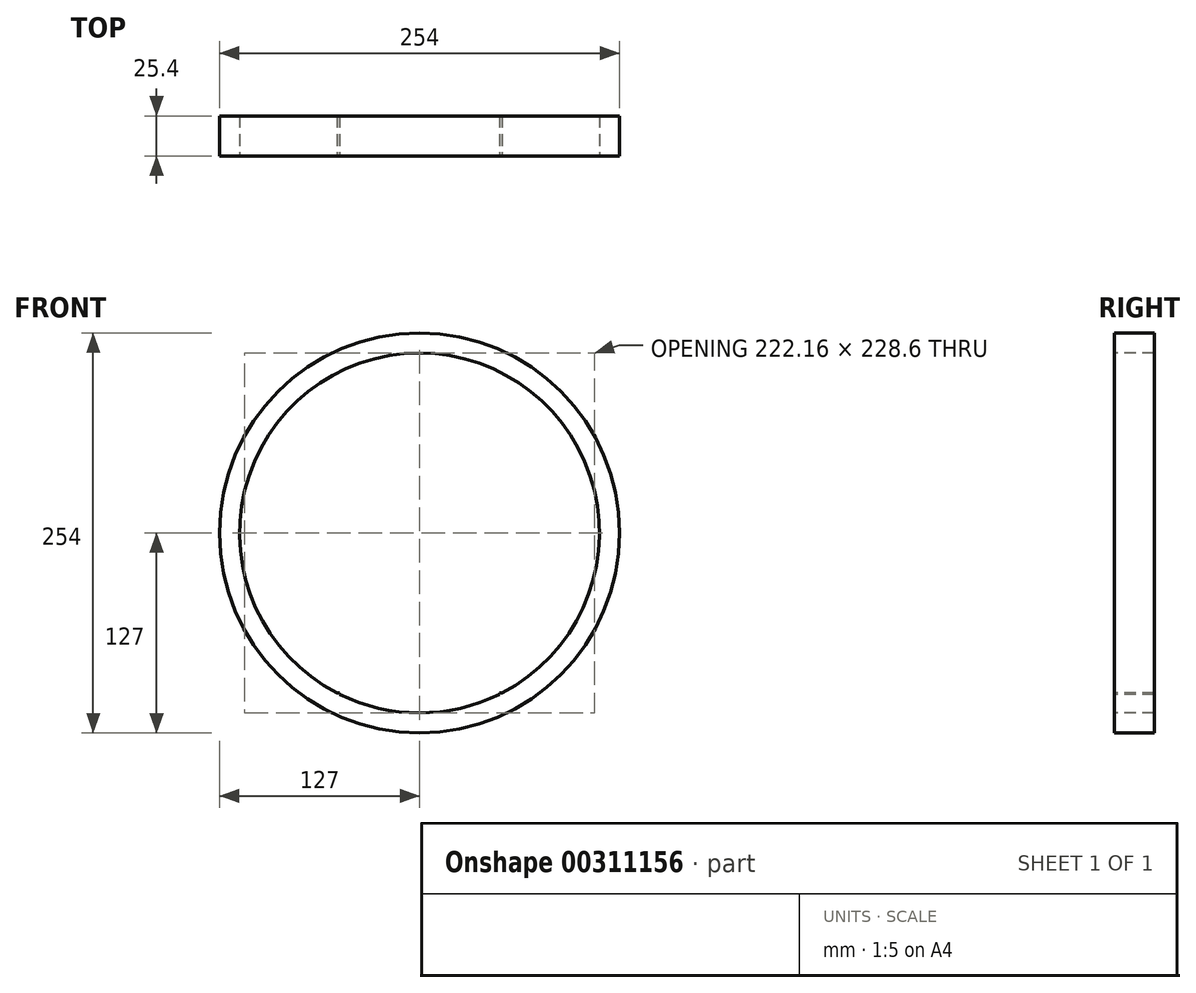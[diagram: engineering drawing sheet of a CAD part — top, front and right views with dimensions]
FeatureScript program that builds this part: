
annotation { "Feature Type Name" : "Feature", "Feature Type Description" : "" }
export const myFeature = defineFeature(function(context is Context, id is Id, definition is map)
    precondition{}
    {
        {
            var Q0;
            Q0=qCreatedBy(makeId("Front.planeOp"),FACE);
            var sketch = newSketch(context, id + "F0", { "sketchPlane" : qUnion([Q0])});
            skCircle(sketch, "E0", {"center": v(0, 0) * mm, "radius": 127 * mm});
            skSolve(sketch);
        }
        {
            var Q0;
            Q0=makeQuery(id+"F0.imprint","IMPRINT",FACE,{"disambiguationData":[TD([[makeQuery(id+"F0.imprint","IMPRINT",EDGE,{"derivedFrom":sQuery(id+"F0.wireOp",EDGE,"E0")}),1.0]])]});
            extrude(context, id + "F1", {"entities" : qUnion([Q0]), "depth" : 25.4 * mm});
        }
        {
            var Q0;
            Q0=makeQuery(id+"F1.opExtrude","CAP_FACE",FACE,{"disambiguationData":[OSD([sQuery(id+"F0.wireOp",EDGE,"E0")])],"isStart":false});
            var sketch = newSketch(context, id + "F2", { "sketchPlane" : qUnion([Q0])});
            skCircle(sketch, "E1", {"center": v(0, 0) * mm, "radius": 114.3 * mm});
            skLineSegment(sketch, "E2", {"start": v(0, 0) * mm, "end": v(25.4, 0) * mm});
            skLineSegment(sketch, "E3", {"start": v(25.4, 0) * mm, "end": v(50.8, 0) * mm});
            skLineSegment(sketch, "E4", {"start": v(50.8, 0) * mm, "end": v(76.2, 0) * mm});
            skLineSegment(sketch, "E5", {"start": v(76.2, 0) * mm, "end": v(101.6, 0) * mm});
            skLineSegment(sketch, "E6", {"start": v(101.6, 0) * mm, "end": v(114.3, 0) * mm});
            skLineSegment(sketch, "E7", {"start": v(25.4, 0) * mm, "end": v(25.4, -111.44) * mm});
            skLineSegment(sketch, "E8", {"start": v(25.4, 0) * mm, "end": v(25.4, 111.44) * mm});
            skLineSegment(sketch, "E9", {"start": v(50.8, 0) * mm, "end": v(50.8, 102.4) * mm});
            skLineSegment(sketch, "E10", {"start": v(50.8, 0) * mm, "end": v(50.8, -102.4) * mm});
            skLineSegment(sketch, "E11", {"start": v(76.2, 0) * mm, "end": v(76.2, 85.2) * mm});
            skLineSegment(sketch, "E12", {"start": v(76.2, 0) * mm, "end": v(76.2, -85.2) * mm});
            skLineSegment(sketch, "E13", {"start": v(101.6, 0) * mm, "end": v(101.6, 52.36) * mm});
            skLineSegment(sketch, "E14", {"start": v(101.6, 0) * mm, "end": v(101.6, -52.36) * mm});
            skPoint(sketch, "E15.orphan", {"position": v(0, 114.3) * mm});
            skLineSegment(sketch, "E16", {"start": v(0, 0) * mm, "end": v(0, 25.4) * mm});
            skLineSegment(sketch, "E17", {"start": v(0, 25.4) * mm, "end": v(0, 50.8) * mm});
            skLineSegment(sketch, "E18", {"start": v(0, 50.8) * mm, "end": v(0, 76.2) * mm});
            skLineSegment(sketch, "E19", {"start": v(0, 76.2) * mm, "end": v(0, 101.6) * mm});
            skLineSegment(sketch, "E20", {"start": v(0, 101.6) * mm, "end": v(0, 114.3) * mm});
            skLineSegment(sketch, "E21", {"start": v(0, 0) * mm, "end": v(0, -25.4) * mm});
            skPoint(sketch, "E21.endSnap0", {"position": v(0, 107.95) * mm});
            skLineSegment(sketch, "E22", {"start": v(0, -25.4) * mm, "end": v(0, -50.8) * mm});
            skLineSegment(sketch, "E23", {"start": v(0, -50.8) * mm, "end": v(0, -76.2) * mm});
            skLineSegment(sketch, "E24", {"start": v(0, -76.2) * mm, "end": v(0, -101.6) * mm});
            skLineSegment(sketch, "E25", {"start": v(0, -101.6) * mm, "end": v(0, -114.3) * mm});
            skLineSegment(sketch, "E26", {"start": v(0, 101.6) * mm, "end": v(50.8, 101.6) * mm});
            skLineSegment(sketch, "E27", {"start": v(0, 76.2) * mm, "end": v(85.2, 76.2) * mm});
            skLineSegment(sketch, "E28", {"start": v(0, 50.8) * mm, "end": v(101.6, 52.36) * mm});
            skLineSegment(sketch, "E29", {"start": v(0, 25.4) * mm, "end": v(111.44, 25.4) * mm});
            skLineSegment(sketch, "E30", {"start": v(0, -25.4) * mm, "end": v(111.44, -25.4) * mm});
            skLineSegment(sketch, "E31", {"start": v(0, -76.2) * mm, "end": v(85.2, -76.2) * mm});
            skLineSegment(sketch, "E32", {"start": v(0, -101.6) * mm, "end": v(52.36, -101.6) * mm});
            skLineSegment(sketch, "E33.MirrorCS", {"start": v(-25.4, 0) * mm, "end": v(-25.4, 111.44) * mm});
            skLineSegment(sketch, "E34.MirrorCS", {"start": v(0, 101.6) * mm, "end": v(-50.8, 101.6) * mm});
            skLineSegment(sketch, "E35.MirrorCS", {"start": v(0, 76.2) * mm, "end": v(-85.2, 76.2) * mm});
            skLineSegment(sketch, "E36.MirrorCS", {"start": v(0, 50.8) * mm, "end": v(-101.6, 52.36) * mm});
            skLineSegment(sketch, "E37.MirrorCS", {"start": v(0, 25.4) * mm, "end": v(-111.44, 25.4) * mm});
            skLineSegment(sketch, "E38.MirrorCS", {"start": v(0, 0) * mm, "end": v(-25.4, 0) * mm});
            skLineSegment(sketch, "E39.MirrorCS", {"start": v(0, -25.4) * mm, "end": v(-111.44, -25.4) * mm});
            skLineSegment(sketch, "E40.MirrorCS", {"start": v(0, -76.2) * mm, "end": v(-85.2, -76.2) * mm});
            skLineSegment(sketch, "E41.MirrorCS", {"start": v(0, -101.6) * mm, "end": v(-52.36, -101.6) * mm});
            skLineSegment(sketch, "E42.MirrorCS", {"start": v(-25.4, 0) * mm, "end": v(-25.4, -111.44) * mm});
            skLineSegment(sketch, "E43.MirrorCS", {"start": v(-50.8, 0) * mm, "end": v(-50.8, -102.4) * mm});
            skLineSegment(sketch, "E44.MirrorCS", {"start": v(-76.2, 0) * mm, "end": v(-76.2, -85.2) * mm});
            skLineSegment(sketch, "E45.MirrorCS", {"start": v(-101.6, 0) * mm, "end": v(-101.6, -52.36) * mm});
            skLineSegment(sketch, "E46.MirrorCS", {"start": v(-101.6, 0) * mm, "end": v(-101.6, 52.36) * mm});
            skLineSegment(sketch, "E47.MirrorCS", {"start": v(-76.2, 0) * mm, "end": v(-76.2, 85.2) * mm});
            skLineSegment(sketch, "E48.MirrorCS", {"start": v(-50.8, 0) * mm, "end": v(-50.8, 102.4) * mm});
            skLineSegment(sketch, "E49.MirrorCS", {"start": v(-25.4, 0) * mm, "end": v(-50.8, 0) * mm});
            skLineSegment(sketch, "E50.MirrorCS", {"start": v(-50.8, 0) * mm, "end": v(-76.2, 0) * mm});
            skLineSegment(sketch, "E51.MirrorCS", {"start": v(-76.2, 0) * mm, "end": v(-101.6, 0) * mm});
            skLineSegment(sketch, "E52.MirrorCS", {"start": v(-101.6, 0) * mm, "end": v(-114.3, 0) * mm});
            skLineSegment(sketch, "E53", {"start": v(0, -50.8) * mm, "end": v(101.6, -50.8) * mm});
            skLineSegment(sketch, "E54", {"start": v(0, -50.8) * mm, "end": v(-101.6, -50.8) * mm});
            skSolve(sketch);
        }
        {
            var Q0;
            {var subQ0=sQuery(id+"F2.wireOp",EDGE,"E48.MirrorCS");var subQ1=sQuery(id+"F2.wireOp",EDGE,"E34.MirrorCS");var subQ2=makeQuery(id+"F2.imprint","INTERSECT",VERTEX,{"derivedFrom":[subQ1,subQ0]});Q0=makeQuery(id+"F2.imprint","IMPRINT",FACE,{"disambiguationData":[TD([[makeQuery(id+"F2.imprint","IMPRINT",EDGE,{"disambiguationData":[TD([[subQ2,1.0]])],"derivedFrom":subQ1}),1.0]])]});}
            var Q1;
            {var subQ0=sQuery(id+"F2.wireOp",EDGE,"E19");Q1=makeQuery(id+"F2.imprint","IMPRINT",FACE,{"disambiguationData":[TD([[makeQuery(id+"F2.imprint","IMPRINT",EDGE,{"derivedFrom":subQ0}),1.0]])]});}
            var Q2;
            {var subQ5=sQuery(id+"F2.wireOp",EDGE,"E19");Q2=makeQuery(id+"F2.imprint","IMPRINT",FACE,{"disambiguationData":[TD([[makeQuery(id+"F2.imprint","IMPRINT",EDGE,{"derivedFrom":subQ5}),-1.0]])]});}
            var Q3;
            {var subQ0=sQuery(id+"F2.wireOp",EDGE,"E27");var subQ1=sQuery(id+"F2.wireOp",EDGE,"E8");var subQ2=makeQuery(id+"F2.imprint","INTERSECT",VERTEX,{"derivedFrom":[subQ1,subQ0]});Q3=makeQuery(id+"F2.imprint","IMPRINT",FACE,{"disambiguationData":[TD([[makeQuery(id+"F2.imprint","IMPRINT",EDGE,{"disambiguationData":[TD([[subQ2,-1.0]])],"derivedFrom":subQ1}),-1.0]])]});}
            var Q4;
            {var subQ0=sQuery(id+"F2.wireOp",EDGE,"E28");var subQ1=sQuery(id+"F2.wireOp",EDGE,"E8");var subQ2=makeQuery(id+"F2.imprint","INTERSECT",VERTEX,{"derivedFrom":[subQ1,subQ0]});Q4=makeQuery(id+"F2.imprint","IMPRINT",FACE,{"disambiguationData":[TD([[makeQuery(id+"F2.imprint","IMPRINT",EDGE,{"disambiguationData":[TD([[subQ2,-1.0]])],"derivedFrom":subQ1}),-1.0]])]});}
            var Q5;
            {var subQ0=sQuery(id+"F2.wireOp",EDGE,"E28");var subQ1=sQuery(id+"F2.wireOp",EDGE,"E9");var subQ2=makeQuery(id+"F2.imprint","INTERSECT",VERTEX,{"derivedFrom":[subQ1,subQ0]});Q5=makeQuery(id+"F2.imprint","IMPRINT",FACE,{"disambiguationData":[TD([[makeQuery(id+"F2.imprint","IMPRINT",EDGE,{"disambiguationData":[TD([[subQ2,-1.0]])],"derivedFrom":subQ1}),-1.0]])]});}
            var Q6;
            {var subQ0=sQuery(id+"F2.wireOp",EDGE,"E29");var subQ1=sQuery(id+"F2.wireOp",EDGE,"E9");var subQ2=makeQuery(id+"F2.imprint","INTERSECT",VERTEX,{"derivedFrom":[subQ1,subQ0]});Q6=makeQuery(id+"F2.imprint","IMPRINT",FACE,{"disambiguationData":[TD([[makeQuery(id+"F2.imprint","IMPRINT",EDGE,{"disambiguationData":[TD([[subQ2,-1.0]])],"derivedFrom":subQ1}),-1.0]])]});}
            var Q7;
            {var subQ0=sQuery(id+"F2.wireOp",EDGE,"E4");Q7=makeQuery(id+"F2.imprint","IMPRINT",FACE,{"disambiguationData":[TD([[makeQuery(id+"F2.imprint","IMPRINT",EDGE,{"derivedFrom":subQ0}),1.0]])]});}
            var Q8;
            {var subQ0=sQuery(id+"F2.wireOp",EDGE,"E29");var subQ1=sQuery(id+"F2.wireOp",EDGE,"E11");var subQ2=makeQuery(id+"F2.imprint","INTERSECT",VERTEX,{"derivedFrom":[subQ1,subQ0]});Q8=makeQuery(id+"F2.imprint","IMPRINT",FACE,{"disambiguationData":[TD([[makeQuery(id+"F2.imprint","IMPRINT",EDGE,{"disambiguationData":[TD([[subQ2,-1.0]])],"derivedFrom":subQ1}),-1.0]])]});}
            var Q9;
            {var subQ0=sQuery(id+"F2.wireOp",EDGE,"E5");Q9=makeQuery(id+"F2.imprint","IMPRINT",FACE,{"disambiguationData":[TD([[makeQuery(id+"F2.imprint","IMPRINT",EDGE,{"derivedFrom":subQ0}),1.0]])]});}
            var Q10;
            {var subQ0=sQuery(id+"F2.wireOp",EDGE,"E5");Q10=makeQuery(id+"F2.imprint","IMPRINT",FACE,{"disambiguationData":[TD([[makeQuery(id+"F2.imprint","IMPRINT",EDGE,{"derivedFrom":subQ0}),-1.0]])]});}
            var Q11;
            {var subQ0=sQuery(id+"F2.wireOp",EDGE,"E30");var subQ1=sQuery(id+"F2.wireOp",EDGE,"E12");var subQ2=makeQuery(id+"F2.imprint","INTERSECT",VERTEX,{"derivedFrom":[subQ1,subQ0]});Q11=makeQuery(id+"F2.imprint","IMPRINT",FACE,{"disambiguationData":[TD([[makeQuery(id+"F2.imprint","IMPRINT",EDGE,{"disambiguationData":[TD([[subQ2,-1.0]])],"derivedFrom":subQ1}),1.0]])]});}
            var Q12;
            {var subQ0=sQuery(id+"F2.wireOp",EDGE,"E30");var subQ1=sQuery(id+"F2.wireOp",EDGE,"E10");var subQ2=makeQuery(id+"F2.imprint","INTERSECT",VERTEX,{"derivedFrom":[subQ1,subQ0]});Q12=makeQuery(id+"F2.imprint","IMPRINT",FACE,{"disambiguationData":[TD([[makeQuery(id+"F2.imprint","IMPRINT",EDGE,{"disambiguationData":[TD([[subQ2,-1.0]])],"derivedFrom":subQ1}),1.0]])]});}
            var Q13;
            {var subQ0=sQuery(id+"F2.wireOp",EDGE,"E53");var subQ1=sQuery(id+"F2.wireOp",EDGE,"E10");var subQ2=makeQuery(id+"F2.imprint","INTERSECT",VERTEX,{"derivedFrom":[subQ1,subQ0]});Q13=makeQuery(id+"F2.imprint","IMPRINT",FACE,{"disambiguationData":[TD([[makeQuery(id+"F2.imprint","IMPRINT",EDGE,{"disambiguationData":[TD([[subQ2,-1.0]])],"derivedFrom":subQ1}),1.0]])]});}
            var Q14;
            {var subQ0=sQuery(id+"F2.wireOp",EDGE,"E31");var subQ1=sQuery(id+"F2.wireOp",EDGE,"E7");var subQ2=makeQuery(id+"F2.imprint","INTERSECT",VERTEX,{"derivedFrom":[subQ1,subQ0]});Q14=makeQuery(id+"F2.imprint","IMPRINT",FACE,{"disambiguationData":[TD([[makeQuery(id+"F2.imprint","IMPRINT",EDGE,{"disambiguationData":[TD([[subQ2,-1.0]])],"derivedFrom":subQ1}),1.0]])]});}
            var Q15;
            {var subQ0=sQuery(id+"F2.wireOp",EDGE,"E53");var subQ1=sQuery(id+"F2.wireOp",EDGE,"E7");var subQ2=makeQuery(id+"F2.imprint","INTERSECT",VERTEX,{"derivedFrom":[subQ1,subQ0]});Q15=makeQuery(id+"F2.imprint","IMPRINT",FACE,{"disambiguationData":[TD([[makeQuery(id+"F2.imprint","IMPRINT",EDGE,{"disambiguationData":[TD([[subQ2,-1.0]])],"derivedFrom":subQ1}),1.0]])]});}
            var Q16;
            {var subQ5=sQuery(id+"F2.wireOp",EDGE,"E24");Q16=makeQuery(id+"F2.imprint","IMPRINT",FACE,{"disambiguationData":[TD([[makeQuery(id+"F2.imprint","IMPRINT",EDGE,{"derivedFrom":subQ5}),1.0]])]});}
            var Q17;
            {var subQ0=sQuery(id+"F2.wireOp",EDGE,"E24");Q17=makeQuery(id+"F2.imprint","IMPRINT",FACE,{"disambiguationData":[TD([[makeQuery(id+"F2.imprint","IMPRINT",EDGE,{"derivedFrom":subQ0}),-1.0]])]});}
            var Q18;
            {var subQ0=sQuery(id+"F2.wireOp",EDGE,"E42.MirrorCS");var subQ1=sQuery(id+"F2.wireOp",EDGE,"E40.MirrorCS");var subQ2=makeQuery(id+"F2.imprint","INTERSECT",VERTEX,{"derivedFrom":[subQ1,subQ0]});Q18=makeQuery(id+"F2.imprint","IMPRINT",FACE,{"disambiguationData":[TD([[makeQuery(id+"F2.imprint","IMPRINT",EDGE,{"disambiguationData":[TD([[subQ2,-1.0]])],"derivedFrom":subQ1}),1.0]])]});}
            var Q19;
            {var subQ0=sQuery(id+"F2.wireOp",EDGE,"E42.MirrorCS");var subQ1=sQuery(id+"F2.wireOp",EDGE,"E40.MirrorCS");var subQ2=makeQuery(id+"F2.imprint","INTERSECT",VERTEX,{"derivedFrom":[subQ1,subQ0]});Q19=makeQuery(id+"F2.imprint","IMPRINT",FACE,{"disambiguationData":[TD([[makeQuery(id+"F2.imprint","IMPRINT",EDGE,{"disambiguationData":[TD([[subQ2,-1.0]])],"derivedFrom":subQ1}),-1.0]])]});}
            var Q20;
            {var subQ0=sQuery(id+"F2.wireOp",EDGE,"E43.MirrorCS");var subQ1=sQuery(id+"F2.wireOp",EDGE,"E40.MirrorCS");var subQ2=makeQuery(id+"F2.imprint","INTERSECT",VERTEX,{"derivedFrom":[subQ1,subQ0]});Q20=makeQuery(id+"F2.imprint","IMPRINT",FACE,{"disambiguationData":[TD([[makeQuery(id+"F2.imprint","IMPRINT",EDGE,{"disambiguationData":[TD([[subQ2,-1.0]])],"derivedFrom":subQ1}),-1.0]])]});}
            var Q21;
            {var subQ0=sQuery(id+"F2.wireOp",EDGE,"E43.MirrorCS");var subQ1=sQuery(id+"F2.wireOp",EDGE,"E39.MirrorCS");var subQ2=makeQuery(id+"F2.imprint","INTERSECT",VERTEX,{"derivedFrom":[subQ1,subQ0]});Q21=makeQuery(id+"F2.imprint","IMPRINT",FACE,{"disambiguationData":[TD([[makeQuery(id+"F2.imprint","IMPRINT",EDGE,{"disambiguationData":[TD([[subQ2,-1.0]])],"derivedFrom":subQ1}),1.0]])]});}
            var Q22;
            {var subQ5=sQuery(id+"F2.wireOp",EDGE,"E50.MirrorCS");Q22=makeQuery(id+"F2.imprint","IMPRINT",FACE,{"disambiguationData":[TD([[makeQuery(id+"F2.imprint","IMPRINT",EDGE,{"derivedFrom":subQ5}),1.0]])]});}
            var Q23;
            {var subQ5=sQuery(id+"F2.wireOp",EDGE,"E51.MirrorCS");Q23=makeQuery(id+"F2.imprint","IMPRINT",FACE,{"disambiguationData":[TD([[makeQuery(id+"F2.imprint","IMPRINT",EDGE,{"derivedFrom":subQ5}),1.0]])]});}
            var Q24;
            {var subQ5=sQuery(id+"F2.wireOp",EDGE,"E51.MirrorCS");Q24=makeQuery(id+"F2.imprint","IMPRINT",FACE,{"disambiguationData":[TD([[makeQuery(id+"F2.imprint","IMPRINT",EDGE,{"derivedFrom":subQ5}),-1.0]])]});}
            var Q25;
            {var subQ5=sQuery(id+"F2.wireOp",EDGE,"E50.MirrorCS");Q25=makeQuery(id+"F2.imprint","IMPRINT",FACE,{"disambiguationData":[TD([[makeQuery(id+"F2.imprint","IMPRINT",EDGE,{"derivedFrom":subQ5}),-1.0]])]});}
            var Q26;
            {var subQ3=sQuery(id+"F2.wireOp",EDGE,"E47.MirrorCS");var subQ5=sQuery(id+"F2.wireOp",EDGE,"E37.MirrorCS");var subQ6=makeQuery(id+"F2.imprint","INTERSECT",VERTEX,{"derivedFrom":[subQ5,subQ3]});Q26=makeQuery(id+"F2.imprint","IMPRINT",FACE,{"disambiguationData":[TD([[makeQuery(id+"F2.imprint","IMPRINT",EDGE,{"disambiguationData":[TD([[subQ6,-1.0]])],"derivedFrom":subQ5}),-1.0]])]});}
            var Q27;
            {var subQ0=sQuery(id+"F2.wireOp",EDGE,"E48.MirrorCS");var subQ1=sQuery(id+"F2.wireOp",EDGE,"E35.MirrorCS");var subQ2=makeQuery(id+"F2.imprint","INTERSECT",VERTEX,{"derivedFrom":[subQ1,subQ0]});Q27=makeQuery(id+"F2.imprint","IMPRINT",FACE,{"disambiguationData":[TD([[makeQuery(id+"F2.imprint","IMPRINT",EDGE,{"disambiguationData":[TD([[subQ2,-1.0]])],"derivedFrom":subQ1}),1.0]])]});}
            var Q28;
            {var subQ0=sQuery(id+"F2.wireOp",EDGE,"E33.MirrorCS");var subQ1=sQuery(id+"F2.wireOp",EDGE,"E35.MirrorCS");var subQ2=makeQuery(id+"F2.imprint","INTERSECT",VERTEX,{"derivedFrom":[subQ1,subQ0]});Q28=makeQuery(id+"F2.imprint","IMPRINT",FACE,{"disambiguationData":[TD([[makeQuery(id+"F2.imprint","IMPRINT",EDGE,{"disambiguationData":[TD([[subQ2,-1.0]])],"derivedFrom":subQ1}),1.0]])]});}
            var Q29;
            {var subQ0=sQuery(id+"F2.wireOp",EDGE,"E18");Q29=makeQuery(id+"F2.imprint","IMPRINT",FACE,{"disambiguationData":[TD([[makeQuery(id+"F2.imprint","IMPRINT",EDGE,{"derivedFrom":subQ0}),1.0]])]});}
            var Q30;
            {var subQ5=sQuery(id+"F2.wireOp",EDGE,"E18");Q30=makeQuery(id+"F2.imprint","IMPRINT",FACE,{"disambiguationData":[TD([[makeQuery(id+"F2.imprint","IMPRINT",EDGE,{"derivedFrom":subQ5}),-1.0]])]});}
            var Q31;
            {var subQ5=sQuery(id+"F2.wireOp",EDGE,"E17");Q31=makeQuery(id+"F2.imprint","IMPRINT",FACE,{"disambiguationData":[TD([[makeQuery(id+"F2.imprint","IMPRINT",EDGE,{"derivedFrom":subQ5}),-1.0]])]});}
            var Q32;
            {var subQ0=sQuery(id+"F2.wireOp",EDGE,"E33.MirrorCS");var subQ1=sQuery(id+"F2.wireOp",EDGE,"E36.MirrorCS");var subQ2=makeQuery(id+"F2.imprint","INTERSECT",VERTEX,{"derivedFrom":[subQ1,subQ0]});Q32=makeQuery(id+"F2.imprint","IMPRINT",FACE,{"disambiguationData":[TD([[makeQuery(id+"F2.imprint","IMPRINT",EDGE,{"disambiguationData":[TD([[subQ2,-1.0]])],"derivedFrom":subQ1}),1.0]])]});}
            var Q33;
            {var subQ0=sQuery(id+"F2.wireOp",EDGE,"E48.MirrorCS");var subQ1=sQuery(id+"F2.wireOp",EDGE,"E36.MirrorCS");var subQ2=makeQuery(id+"F2.imprint","INTERSECT",VERTEX,{"derivedFrom":[subQ1,subQ0]});Q33=makeQuery(id+"F2.imprint","IMPRINT",FACE,{"disambiguationData":[TD([[makeQuery(id+"F2.imprint","IMPRINT",EDGE,{"disambiguationData":[TD([[subQ2,-1.0]])],"derivedFrom":subQ1}),1.0]])]});}
            var Q34;
            {var subQ0=sQuery(id+"F2.wireOp",EDGE,"E17");Q34=makeQuery(id+"F2.imprint","IMPRINT",FACE,{"disambiguationData":[TD([[makeQuery(id+"F2.imprint","IMPRINT",EDGE,{"derivedFrom":subQ0}),1.0]])]});}
            var Q35;
            {var subQ0=sQuery(id+"F2.wireOp",EDGE,"E29");var subQ1=sQuery(id+"F2.wireOp",EDGE,"E8");var subQ2=makeQuery(id+"F2.imprint","INTERSECT",VERTEX,{"derivedFrom":[subQ1,subQ0]});Q35=makeQuery(id+"F2.imprint","IMPRINT",FACE,{"disambiguationData":[TD([[makeQuery(id+"F2.imprint","IMPRINT",EDGE,{"disambiguationData":[TD([[subQ2,-1.0]])],"derivedFrom":subQ1}),-1.0]])]});}
            var Q36;
            {var subQ0=sQuery(id+"F2.wireOp",EDGE,"E3");Q36=makeQuery(id+"F2.imprint","IMPRINT",FACE,{"disambiguationData":[TD([[makeQuery(id+"F2.imprint","IMPRINT",EDGE,{"derivedFrom":subQ0}),1.0]])]});}
            var Q37;
            {var subQ0=sQuery(id+"F2.wireOp",EDGE,"E2");Q37=makeQuery(id+"F2.imprint","IMPRINT",FACE,{"disambiguationData":[TD([[makeQuery(id+"F2.imprint","IMPRINT",EDGE,{"derivedFrom":subQ0}),1.0]])]});}
            var Q38;
            {var subQ0=sQuery(id+"F2.wireOp",EDGE,"E16");Q38=makeQuery(id+"F2.imprint","IMPRINT",FACE,{"disambiguationData":[TD([[makeQuery(id+"F2.imprint","IMPRINT",EDGE,{"derivedFrom":subQ0}),1.0]])]});}
            var Q39;
            {var subQ5=sQuery(id+"F2.wireOp",EDGE,"E49.MirrorCS");Q39=makeQuery(id+"F2.imprint","IMPRINT",FACE,{"disambiguationData":[TD([[makeQuery(id+"F2.imprint","IMPRINT",EDGE,{"derivedFrom":subQ5}),1.0]])]});}
            var Q40;
            {var subQ0=sQuery(id+"F2.wireOp",EDGE,"E21");Q40=makeQuery(id+"F2.imprint","IMPRINT",FACE,{"disambiguationData":[TD([[makeQuery(id+"F2.imprint","IMPRINT",EDGE,{"derivedFrom":subQ0}),-1.0]])]});}
            var Q41;
            {var subQ0=sQuery(id+"F2.wireOp",EDGE,"E2");Q41=makeQuery(id+"F2.imprint","IMPRINT",FACE,{"disambiguationData":[TD([[makeQuery(id+"F2.imprint","IMPRINT",EDGE,{"derivedFrom":subQ0}),-1.0]])]});}
            var Q42;
            {var subQ0=sQuery(id+"F2.wireOp",EDGE,"E3");Q42=makeQuery(id+"F2.imprint","IMPRINT",FACE,{"disambiguationData":[TD([[makeQuery(id+"F2.imprint","IMPRINT",EDGE,{"derivedFrom":subQ0}),-1.0]])]});}
            var Q43;
            {var subQ0=sQuery(id+"F2.wireOp",EDGE,"E4");Q43=makeQuery(id+"F2.imprint","IMPRINT",FACE,{"disambiguationData":[TD([[makeQuery(id+"F2.imprint","IMPRINT",EDGE,{"derivedFrom":subQ0}),-1.0]])]});}
            var Q44;
            {var subQ0=sQuery(id+"F2.wireOp",EDGE,"E30");var subQ1=sQuery(id+"F2.wireOp",EDGE,"E7");var subQ2=makeQuery(id+"F2.imprint","INTERSECT",VERTEX,{"derivedFrom":[subQ1,subQ0]});Q44=makeQuery(id+"F2.imprint","IMPRINT",FACE,{"disambiguationData":[TD([[makeQuery(id+"F2.imprint","IMPRINT",EDGE,{"disambiguationData":[TD([[subQ2,-1.0]])],"derivedFrom":subQ1}),1.0]])]});}
            var Q45;
            {var subQ5=sQuery(id+"F2.wireOp",EDGE,"E22");Q45=makeQuery(id+"F2.imprint","IMPRINT",FACE,{"disambiguationData":[TD([[makeQuery(id+"F2.imprint","IMPRINT",EDGE,{"derivedFrom":subQ5}),1.0]])]});}
            var Q46;
            {var subQ5=sQuery(id+"F2.wireOp",EDGE,"E23");Q46=makeQuery(id+"F2.imprint","IMPRINT",FACE,{"disambiguationData":[TD([[makeQuery(id+"F2.imprint","IMPRINT",EDGE,{"derivedFrom":subQ5}),1.0]])]});}
            var Q47;
            {var subQ0=sQuery(id+"F2.wireOp",EDGE,"E23");Q47=makeQuery(id+"F2.imprint","IMPRINT",FACE,{"disambiguationData":[TD([[makeQuery(id+"F2.imprint","IMPRINT",EDGE,{"derivedFrom":subQ0}),-1.0]])]});}
            var Q48;
            {var subQ0=sQuery(id+"F2.wireOp",EDGE,"E22");Q48=makeQuery(id+"F2.imprint","IMPRINT",FACE,{"disambiguationData":[TD([[makeQuery(id+"F2.imprint","IMPRINT",EDGE,{"derivedFrom":subQ0}),-1.0]])]});}
            var Q49;
            {var subQ0=sQuery(id+"F2.wireOp",EDGE,"E42.MirrorCS");var subQ1=sQuery(id+"F2.wireOp",EDGE,"E39.MirrorCS");var subQ2=makeQuery(id+"F2.imprint","INTERSECT",VERTEX,{"derivedFrom":[subQ1,subQ0]});Q49=makeQuery(id+"F2.imprint","IMPRINT",FACE,{"disambiguationData":[TD([[makeQuery(id+"F2.imprint","IMPRINT",EDGE,{"disambiguationData":[TD([[subQ2,-1.0]])],"derivedFrom":subQ1}),1.0]])]});}
            var Q50;
            {var subQ0=sQuery(id+"F2.wireOp",EDGE,"E35.MirrorCS");var subQ1=sQuery(id+"F2.wireOp",EDGE,"E1");var subQ2=makeQuery(id+"F2.imprint","INTERSECT",VERTEX,{"derivedFrom":[subQ1,subQ0]});Q50=makeQuery(id+"F2.imprint","IMPRINT",FACE,{"disambiguationData":[TD([[makeQuery(id+"F2.imprint","IMPRINT",EDGE,{"disambiguationData":[TD([[subQ2,1.0]])],"derivedFrom":subQ0}),1.0]])]});}
            var Q51;
            {var subQ0=sQuery(id+"F2.wireOp",EDGE,"E35.MirrorCS");var subQ1=sQuery(id+"F2.wireOp",EDGE,"E1");var subQ2=makeQuery(id+"F2.imprint","INTERSECT",VERTEX,{"derivedFrom":[subQ1,subQ0]});Q51=makeQuery(id+"F2.imprint","IMPRINT",FACE,{"disambiguationData":[TD([[makeQuery(id+"F2.imprint","IMPRINT",EDGE,{"disambiguationData":[TD([[subQ2,1.0]])],"derivedFrom":subQ1}),1.0]])]});}
            var Q52;
            {var subQ0=sQuery(id+"F2.wireOp",EDGE,"E47.MirrorCS");var subQ1=sQuery(id+"F2.wireOp",EDGE,"E1");var subQ2=makeQuery(id+"F2.imprint","INTERSECT",VERTEX,{"derivedFrom":[subQ1,subQ0]});Q52=makeQuery(id+"F2.imprint","IMPRINT",FACE,{"disambiguationData":[TD([[makeQuery(id+"F2.imprint","IMPRINT",EDGE,{"disambiguationData":[TD([[subQ2,1.0]])],"derivedFrom":subQ1}),1.0]])]});}
            var Q53;
            {var subQ0=sQuery(id+"F2.wireOp",EDGE,"E48.MirrorCS");var subQ1=sQuery(id+"F2.wireOp",EDGE,"E1");var subQ2=makeQuery(id+"F2.imprint","INTERSECT",VERTEX,{"derivedFrom":[subQ1,subQ0]});Q53=makeQuery(id+"F2.imprint","IMPRINT",FACE,{"disambiguationData":[TD([[makeQuery(id+"F2.imprint","IMPRINT",EDGE,{"disambiguationData":[TD([[subQ2,1.0]])],"derivedFrom":subQ1}),1.0]])]});}
            var Q54;
            {var subQ0=sQuery(id+"F2.wireOp",EDGE,"E20");Q54=makeQuery(id+"F2.imprint","IMPRINT",FACE,{"disambiguationData":[TD([[makeQuery(id+"F2.imprint","IMPRINT",EDGE,{"derivedFrom":subQ0}),1.0]])]});}
            var Q55;
            {var subQ3=sQuery(id+"F2.wireOp",EDGE,"E20");Q55=makeQuery(id+"F2.imprint","IMPRINT",FACE,{"disambiguationData":[TD([[makeQuery(id+"F2.imprint","IMPRINT",EDGE,{"derivedFrom":subQ3}),-1.0]])]});}
            var Q56;
            {var subQ0=sQuery(id+"F2.wireOp",EDGE,"E8");var subQ1=sQuery(id+"F2.wireOp",EDGE,"E1");var subQ2=makeQuery(id+"F2.imprint","INTERSECT",VERTEX,{"derivedFrom":[subQ1,subQ0]});Q56=makeQuery(id+"F2.imprint","IMPRINT",FACE,{"disambiguationData":[TD([[makeQuery(id+"F2.imprint","IMPRINT",EDGE,{"disambiguationData":[TD([[subQ2,1.0]])],"derivedFrom":subQ1}),1.0]])]});}
            var Q57;
            {var subQ1=sQuery(id+"F2.wireOp",EDGE,"E1");var subQ5=sQuery(id+"F2.wireOp",EDGE,"E9");var subQ8=makeQuery(id+"F2.imprint","INTERSECT",VERTEX,{"derivedFrom":[subQ1,subQ5]});Q57=makeQuery(id+"F2.imprint","IMPRINT",FACE,{"disambiguationData":[TD([[makeQuery(id+"F2.imprint","IMPRINT",EDGE,{"disambiguationData":[TD([[subQ8,1.0]])],"derivedFrom":subQ1}),1.0]])]});}
            var Q58;
            {var subQ0=sQuery(id+"F2.wireOp",EDGE,"E11");var subQ1=sQuery(id+"F2.wireOp",EDGE,"E1");var subQ2=makeQuery(id+"F2.imprint","INTERSECT",VERTEX,{"derivedFrom":[subQ1,subQ0]});Q58=makeQuery(id+"F2.imprint","IMPRINT",FACE,{"disambiguationData":[TD([[makeQuery(id+"F2.imprint","IMPRINT",EDGE,{"disambiguationData":[TD([[subQ2,1.0]])],"derivedFrom":subQ1}),1.0]])]});}
            var Q59;
            {var subQ0=sQuery(id+"F2.wireOp",EDGE,"E28");var subQ5=sQuery(id+"F2.wireOp",EDGE,"E11");var subQ6=makeQuery(id+"F2.imprint","INTERSECT",VERTEX,{"derivedFrom":[subQ5,subQ0]});Q59=makeQuery(id+"F2.imprint","IMPRINT",FACE,{"disambiguationData":[TD([[makeQuery(id+"F2.imprint","IMPRINT",EDGE,{"disambiguationData":[TD([[subQ6,-1.0]])],"derivedFrom":subQ5}),-1.0]])]});}
            var Q60;
            {var subQ1=sQuery(id+"F2.wireOp",EDGE,"E1");var subQ3=sQuery(id+"F2.wireOp",EDGE,"E29");var subQ4=makeQuery(id+"F2.imprint","INTERSECT",VERTEX,{"derivedFrom":[subQ1,subQ3]});Q60=makeQuery(id+"F2.imprint","IMPRINT",FACE,{"disambiguationData":[TD([[makeQuery(id+"F2.imprint","IMPRINT",EDGE,{"disambiguationData":[TD([[subQ4,1.0]])],"derivedFrom":subQ3}),1.0]])]});}
            var Q61;
            {var subQ0=sQuery(id+"F2.wireOp",EDGE,"E6");Q61=makeQuery(id+"F2.imprint","IMPRINT",FACE,{"disambiguationData":[TD([[makeQuery(id+"F2.imprint","IMPRINT",EDGE,{"derivedFrom":subQ0}),1.0]])]});}
            var Q62;
            {var subQ0=sQuery(id+"F2.wireOp",EDGE,"E6");Q62=makeQuery(id+"F2.imprint","IMPRINT",FACE,{"disambiguationData":[TD([[makeQuery(id+"F2.imprint","IMPRINT",EDGE,{"derivedFrom":subQ0}),-1.0]])]});}
            var Q63;
            {var subQ0=sQuery(id+"F2.wireOp",EDGE,"E14");var subQ1=sQuery(id+"F2.wireOp",EDGE,"E1");var subQ2=makeQuery(id+"F2.imprint","INTERSECT",VERTEX,{"derivedFrom":[subQ1,subQ0]});Q63=makeQuery(id+"F2.imprint","IMPRINT",FACE,{"disambiguationData":[TD([[makeQuery(id+"F2.imprint","IMPRINT",EDGE,{"disambiguationData":[TD([[subQ2,-1.0]])],"derivedFrom":subQ1}),1.0]])]});}
            var Q64;
            {var subQ1=sQuery(id+"F2.wireOp",EDGE,"E1");var subQ5=sQuery(id+"F2.wireOp",EDGE,"E14");var subQ6=makeQuery(id+"F2.imprint","INTERSECT",VERTEX,{"derivedFrom":[subQ1,subQ5]});Q64=makeQuery(id+"F2.imprint","IMPRINT",FACE,{"disambiguationData":[TD([[makeQuery(id+"F2.imprint","IMPRINT",EDGE,{"disambiguationData":[TD([[subQ6,1.0]])],"derivedFrom":subQ1}),1.0]])]});}
            var Q65;
            {var subQ0=sQuery(id+"F2.wireOp",EDGE,"E7");var subQ1=sQuery(id+"F2.wireOp",EDGE,"E1");var subQ2=makeQuery(id+"F2.imprint","INTERSECT",VERTEX,{"derivedFrom":[subQ1,subQ0]});Q65=makeQuery(id+"F2.imprint","IMPRINT",FACE,{"disambiguationData":[TD([[makeQuery(id+"F2.imprint","IMPRINT",EDGE,{"disambiguationData":[TD([[subQ2,-1.0]])],"derivedFrom":subQ1}),1.0]])]});}
            var Q66;
            {var subQ3=sQuery(id+"F2.wireOp",EDGE,"E25");Q66=makeQuery(id+"F2.imprint","IMPRINT",FACE,{"disambiguationData":[TD([[makeQuery(id+"F2.imprint","IMPRINT",EDGE,{"derivedFrom":subQ3}),1.0]])]});}
            var Q67;
            {var subQ0=sQuery(id+"F2.wireOp",EDGE,"E25");Q67=makeQuery(id+"F2.imprint","IMPRINT",FACE,{"disambiguationData":[TD([[makeQuery(id+"F2.imprint","IMPRINT",EDGE,{"derivedFrom":subQ0}),-1.0]])]});}
            var Q68;
            {var subQ0=sQuery(id+"F2.wireOp",EDGE,"E42.MirrorCS");var subQ1=sQuery(id+"F2.wireOp",EDGE,"E1");var subQ2=makeQuery(id+"F2.imprint","INTERSECT",VERTEX,{"derivedFrom":[subQ1,subQ0]});Q68=makeQuery(id+"F2.imprint","IMPRINT",FACE,{"disambiguationData":[TD([[makeQuery(id+"F2.imprint","IMPRINT",EDGE,{"disambiguationData":[TD([[subQ2,1.0]])],"derivedFrom":subQ1}),1.0]])]});}
            var Q69;
            {var subQ3=sQuery(id+"F2.wireOp",EDGE,"E41.MirrorCS");var subQ5=sQuery(id+"F2.wireOp",EDGE,"E1");var subQ6=makeQuery(id+"F2.imprint","INTERSECT",VERTEX,{"derivedFrom":[subQ5,subQ3]});Q69=makeQuery(id+"F2.imprint","IMPRINT",FACE,{"disambiguationData":[TD([[makeQuery(id+"F2.imprint","IMPRINT",EDGE,{"disambiguationData":[TD([[subQ6,1.0]])],"derivedFrom":subQ5}),1.0]])]});}
            var Q70;
            {var subQ0=sQuery(id+"F2.wireOp",EDGE,"E40.MirrorCS");var subQ1=sQuery(id+"F2.wireOp",EDGE,"E1");var subQ2=makeQuery(id+"F2.imprint","INTERSECT",VERTEX,{"derivedFrom":[subQ1,subQ0]});Q70=makeQuery(id+"F2.imprint","IMPRINT",FACE,{"disambiguationData":[TD([[makeQuery(id+"F2.imprint","IMPRINT",EDGE,{"disambiguationData":[TD([[subQ2,-1.0]])],"derivedFrom":subQ1}),1.0]])]});}
            var Q71;
            {var subQ1=sQuery(id+"F2.wireOp",EDGE,"E40.MirrorCS");var subQ6=sQuery(id+"F2.wireOp",EDGE,"E1");var subQ9=makeQuery(id+"F2.imprint","INTERSECT",VERTEX,{"derivedFrom":[subQ6,subQ1]});Q71=makeQuery(id+"F2.imprint","IMPRINT",FACE,{"disambiguationData":[TD([[makeQuery(id+"F2.imprint","IMPRINT",EDGE,{"disambiguationData":[TD([[subQ9,1.0]])],"derivedFrom":subQ6}),1.0]])]});}
            var Q72;
            {var subQ0=sQuery(id+"F2.wireOp",EDGE,"E44.MirrorCS");var subQ1=sQuery(id+"F2.wireOp",EDGE,"E39.MirrorCS");var subQ2=makeQuery(id+"F2.imprint","INTERSECT",VERTEX,{"derivedFrom":[subQ1,subQ0]});Q72=makeQuery(id+"F2.imprint","IMPRINT",FACE,{"disambiguationData":[TD([[makeQuery(id+"F2.imprint","IMPRINT",EDGE,{"disambiguationData":[TD([[subQ2,-1.0]])],"derivedFrom":subQ1}),1.0]])]});}
            var Q73;
            {var subQ0=sQuery(id+"F2.wireOp",EDGE,"E39.MirrorCS");var subQ1=sQuery(id+"F2.wireOp",EDGE,"E1");var subQ2=makeQuery(id+"F2.imprint","INTERSECT",VERTEX,{"derivedFrom":[subQ1,subQ0]});Q73=makeQuery(id+"F2.imprint","IMPRINT",FACE,{"disambiguationData":[TD([[makeQuery(id+"F2.imprint","IMPRINT",EDGE,{"disambiguationData":[TD([[subQ2,-1.0]])],"derivedFrom":subQ1}),1.0]])]});}
            var Q74;
            {var subQ3=sQuery(id+"F2.wireOp",EDGE,"E52.MirrorCS");Q74=makeQuery(id+"F2.imprint","IMPRINT",FACE,{"disambiguationData":[TD([[makeQuery(id+"F2.imprint","IMPRINT",EDGE,{"derivedFrom":subQ3}),1.0]])]});}
            var Q75;
            {var subQ3=sQuery(id+"F2.wireOp",EDGE,"E52.MirrorCS");Q75=makeQuery(id+"F2.imprint","IMPRINT",FACE,{"disambiguationData":[TD([[makeQuery(id+"F2.imprint","IMPRINT",EDGE,{"derivedFrom":subQ3}),-1.0]])]});}
            var Q76;
            {var subQ1=sQuery(id+"F2.wireOp",EDGE,"E1");var subQ3=sQuery(id+"F2.wireOp",EDGE,"E37.MirrorCS");var subQ4=makeQuery(id+"F2.imprint","INTERSECT",VERTEX,{"derivedFrom":[subQ1,subQ3]});Q76=makeQuery(id+"F2.imprint","IMPRINT",FACE,{"disambiguationData":[TD([[makeQuery(id+"F2.imprint","IMPRINT",EDGE,{"disambiguationData":[TD([[subQ4,1.0]])],"derivedFrom":subQ3}),-1.0]])]});}
            var Q77;
            {var subQ5=sQuery(id+"F2.wireOp",EDGE,"E49.MirrorCS");Q77=makeQuery(id+"F2.imprint","IMPRINT",FACE,{"disambiguationData":[TD([[makeQuery(id+"F2.imprint","IMPRINT",EDGE,{"derivedFrom":subQ5}),-1.0]])]});}
            var Q78;
            {var subQ3=sQuery(id+"F2.wireOp",EDGE,"E12");var subQ5=sQuery(id+"F2.wireOp",EDGE,"E1");var subQ6=makeQuery(id+"F2.imprint","INTERSECT",VERTEX,{"derivedFrom":[subQ5,subQ3]});Q78=makeQuery(id+"F2.imprint","IMPRINT",FACE,{"disambiguationData":[TD([[makeQuery(id+"F2.imprint","IMPRINT",EDGE,{"disambiguationData":[TD([[subQ6,1.0]])],"derivedFrom":subQ5}),1.0]])]});}
            var Q79;
            {var subQ0=sQuery(id+"F2.wireOp",EDGE,"E12");var subQ1=sQuery(id+"F2.wireOp",EDGE,"E1");var subQ2=makeQuery(id+"F2.imprint","INTERSECT",VERTEX,{"derivedFrom":[subQ1,subQ0]});Q79=makeQuery(id+"F2.imprint","IMPRINT",FACE,{"disambiguationData":[TD([[makeQuery(id+"F2.imprint","IMPRINT",EDGE,{"disambiguationData":[TD([[subQ2,-1.0]])],"derivedFrom":subQ1}),1.0]])]});}
            extrude(context, id + "F3", {"entities" : qUnion([Q0, Q1, Q2, Q3, Q4, Q5, Q6, Q7, Q8, Q9, Q10, Q11, Q12, Q13, Q14, Q15, Q16, Q17, Q18, Q19, Q20, Q21, Q22, Q23, Q24, Q25, Q26, Q27, Q28, Q29, Q30, Q31, Q32, Q33, Q34, Q35, Q36, Q37, Q38, Q39, Q40, Q41, Q42, Q43, Q44, Q45, Q46, Q47, Q48, Q49, Q50, Q51, Q52, Q53, Q54, Q55, Q56, Q57, Q58, Q59, Q60, Q61, Q62, Q63, Q64, Q65, Q66, Q67, Q68, Q69, Q70, Q71, Q72, Q73, Q74, Q75, Q76, Q77, Q78, Q79]), "operationType" : NewBodyOperationType.REMOVE, "oppositeDirection" : true, "depth" : 25.4 * mm});
        }
    });
